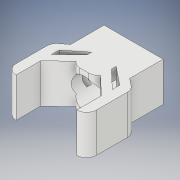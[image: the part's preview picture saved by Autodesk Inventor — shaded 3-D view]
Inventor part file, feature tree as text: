
AUTODESK INVENTOR PART (.ipt)
format: ipt  version: 2017 SP1 (Build 210196100, 196)  size: 199,168 bytes
history: native  units: in
note: dims shown in document units (in); Inventor stores cm internally (conversion verified against a paired STEP export)
features: extrude x4, sketch x4, fillet x1, projected_geometry x1
ambient origin geometry x8: Origin, YZ Plane, XZ Plane, XY Plane, X Axis, Y Axis, Z Axis, Center Point
bodies: Solid1 (feature_tree)
feature tree (10):
  extrude  "Extrusion1"  Depth=0.2362in
  extrude  "Extrusion3"  Depth=0.0787in TaperAngle=0.0deg
  fillet  "Fillet1"  Radius=0.0984in
  extrude  "Extrusion4"  Depth=0.0394in
  extrude  "Extrusion5"  Depth=0.0394in
  sketch  "Sketch1"  dims[d0=0.1181in d1=0.2362in]
  sketch  "Sketch2"  dims[d2=0.1575in d3=0.0787in d4=0.0in d5=0.0984in]
  sketch  "Sketch5"  dims[d6=0.1181in d7=0.0394in]
  sketch  "Sketch6"  dims[d8=0.1969in d11=0.0315in d13=0.1181in d15=0.0315in d18=0.0394in d19=0.1969in d20=0.0315in d21=0.1181in d22=0.0315in d23=0.1575in d24=0.0in d25=0.0394in d27=0.1575in d28=0.0in d29=0.1575in d30=0.0in]
  projected_geometry  "Projected Loop3"
